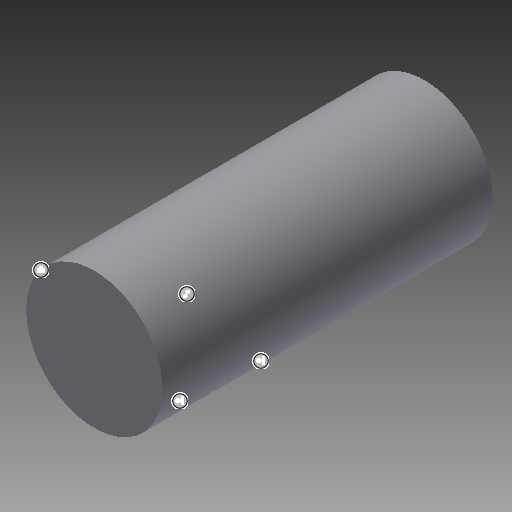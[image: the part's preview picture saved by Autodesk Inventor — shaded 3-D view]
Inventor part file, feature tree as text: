
AUTODESK INVENTOR PART (.ipt)
format: ipt  version: 2018.1 (Build 221171000, 171)  size: 107,008 bytes
history: native  units: mm
features: extrude x1, sketch x1
ambient origin geometry x8: Origin, YZ Plane, XZ Plane, XY Plane, X Axis, Y Axis, Z Axis, Center Point
bodies: Solid1 (feature_tree)
feature tree (2):
  extrude  "Extrusion1"  TaperAngle=0.0deg  [1 undecoded]
  sketch  "Sketch1"  dims[d2=0.0mm d3=0.0mm d4=0.0mm d9=0.0mm d10=0.0mm]
note: 1 required parameter value undecoded (feature->parameter linkage not recoverable at this tier; creation-order binding heuristic only, values carry confidence <= 0.55)
